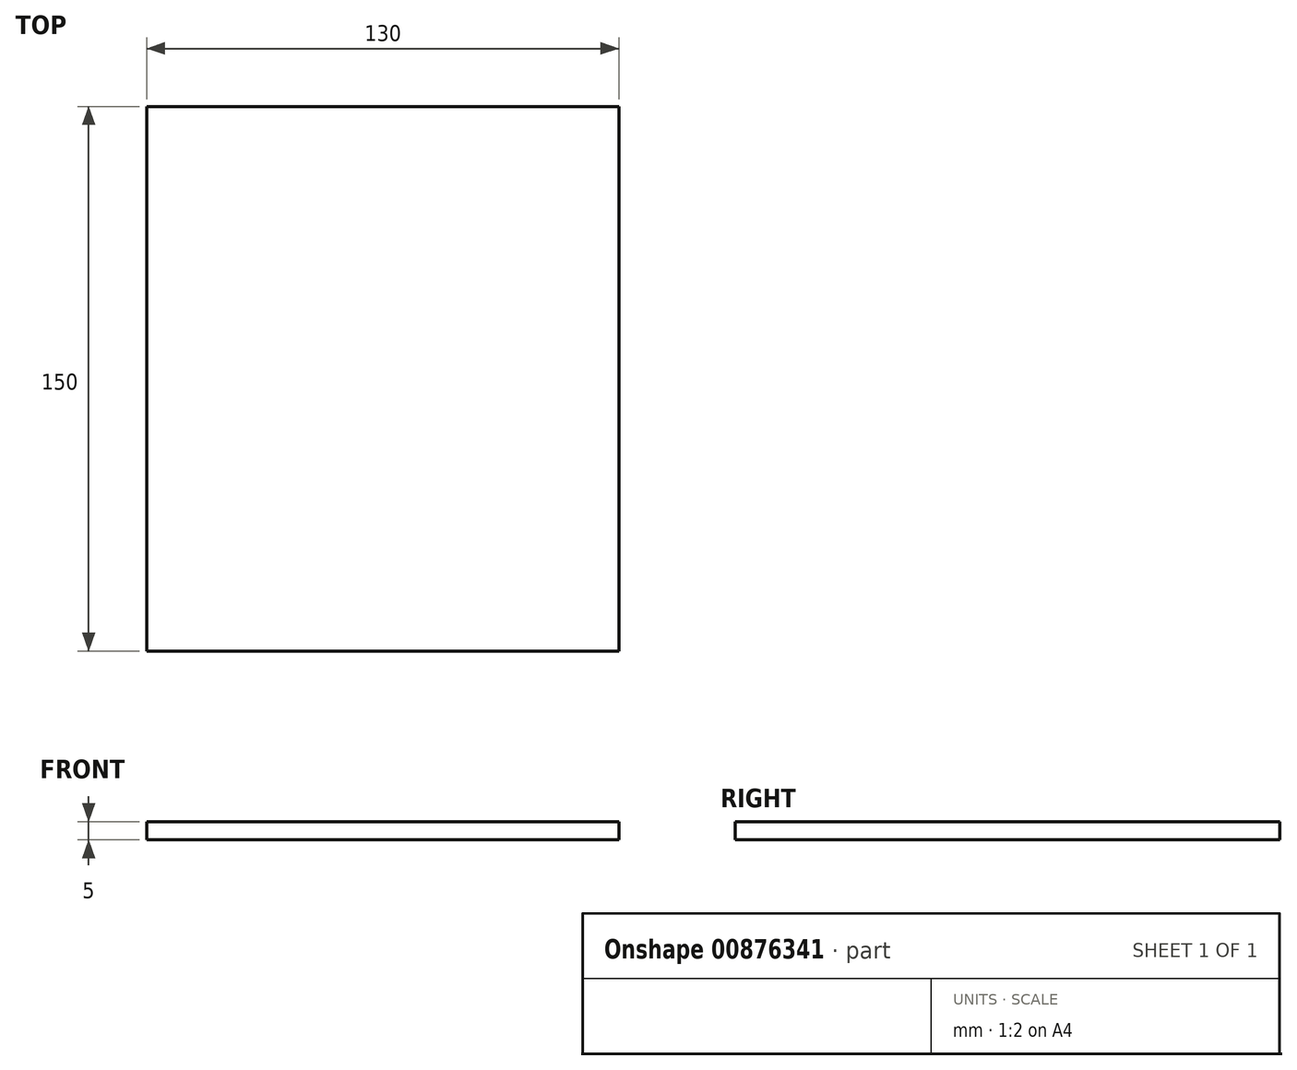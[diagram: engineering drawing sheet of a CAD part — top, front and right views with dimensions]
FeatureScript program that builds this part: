
annotation { "Feature Type Name" : "Feature", "Feature Type Description" : "" }
export const myFeature = defineFeature(function(context is Context, id is Id, definition is map)
    precondition{}
    {
        {
            var Q0;
            Q0=qCreatedBy(makeId("Top.planeOp"),FACE);
            var sketch = newSketch(context, id + "F0", { "sketchPlane" : qUnion([Q0])});
            skLineSegment(sketch, "E0.bottom", {"start": v(-71.76, 95.07) * mm, "end": v(58.24, 95.07) * mm});
            skLineSegment(sketch, "E0.top", {"start": v(-71.76, -54.93) * mm, "end": v(58.24, -54.93) * mm});
            skLineSegment(sketch, "E0.left", {"start": v(-71.76, 95.07) * mm, "end": v(-71.76, -54.93) * mm});
            skLineSegment(sketch, "E0.right", {"start": v(58.24, 95.07) * mm, "end": v(58.24, -54.93) * mm});
            skSolve(sketch);
        }
        {
            var Q0;
            Q0=makeQuery(id+"F0.imprint","IMPRINT",FACE,{"disambiguationData":[TD([[makeQuery(id+"F0.imprint","IMPRINT",EDGE,{"derivedFrom":sQuery(id+"F0.wireOp",EDGE,"E0.bottom")}),-1.0]])]});
            extrude(context, id + "F1", {"entities" : qUnion([Q0]), "depth" : 5 * mm, "offsetDistance" : 25 * mm});
        }
    });
